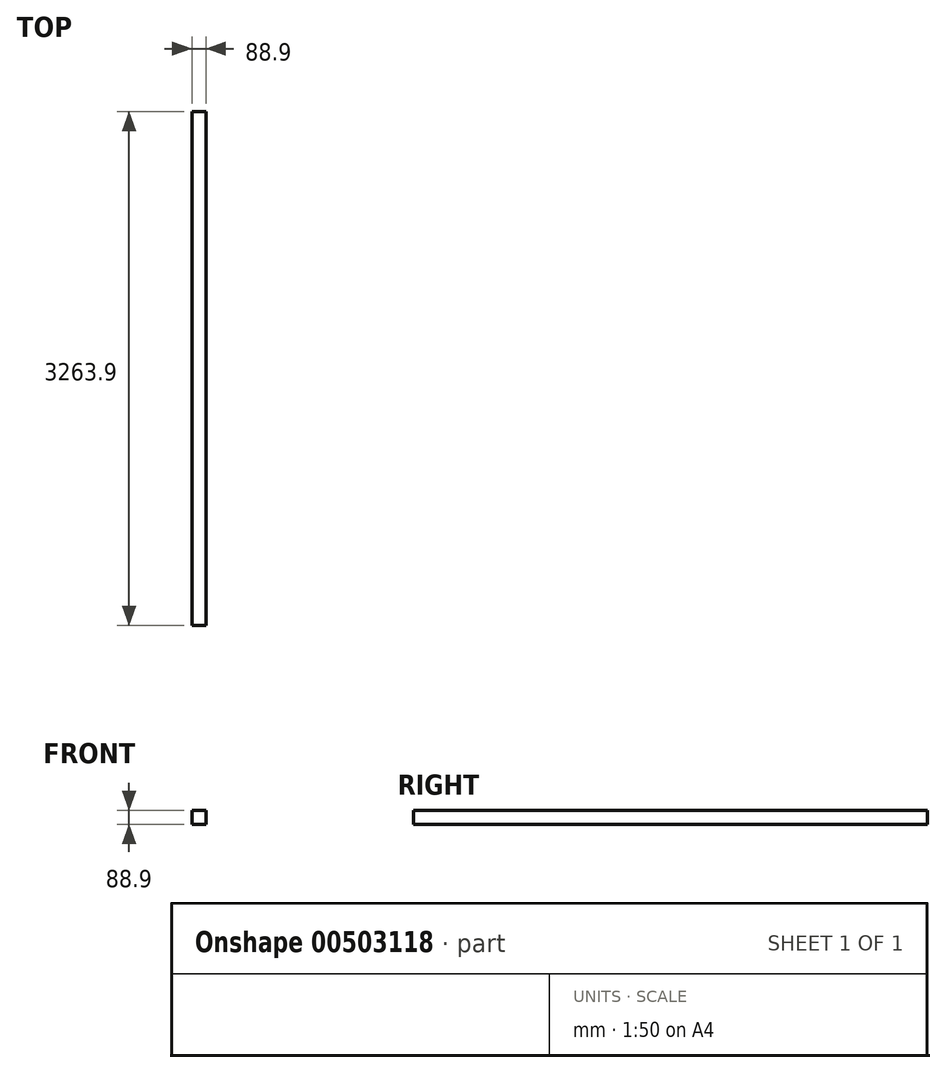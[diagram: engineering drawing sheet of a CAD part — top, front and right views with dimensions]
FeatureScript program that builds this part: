
annotation { "Feature Type Name" : "Feature", "Feature Type Description" : "" }
export const myFeature = defineFeature(function(context is Context, id is Id, definition is map)
    precondition{}
    {
        {
            var Q0;
            Q0=qCreatedBy(makeId("Front.planeOp"),FACE);
            var sketch = newSketch(context, id + "F0", { "sketchPlane" : qUnion([Q0])});
            skLineSegment(sketch, "E0.bottom", {"start": v(0, 0) * mm, "end": v(88.9, 0) * mm});
            skLineSegment(sketch, "E0.top", {"start": v(0, 88.9) * mm, "end": v(88.9, 88.9) * mm});
            skLineSegment(sketch, "E0.left", {"start": v(0, 0) * mm, "end": v(0, 88.9) * mm});
            skLineSegment(sketch, "E0.right", {"start": v(88.9, 0) * mm, "end": v(88.9, 88.9) * mm});
            skSolve(sketch);
        }
        {
            var Q0;
            Q0 = qSketchRegion(id + "F0", true);
            extrude(context, id + "F1", {"entities" : qUnion([Q0]), "depth" : 3263.9 * mm});
        }
    });
